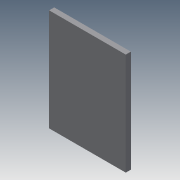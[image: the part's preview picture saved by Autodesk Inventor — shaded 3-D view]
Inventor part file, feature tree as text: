
AUTODESK INVENTOR PART (.ipt)
format: ipt  version: 2015 (Build 190159000, 159)  size: 68,608 bytes
history: native  units: mm
features: extrude x1, sketch x1
ambient origin geometry x8: Origin, YZ Plane, XZ Plane, XY Plane, X Axis, Y Axis, Z Axis, Center Point
bodies: Solid1 (feature_tree)
feature tree (2):
  extrude  "Extrusion1"  Depth=150.0mm
  sketch  "Sketch1"  dims[d0=200.0mm d1=150.0mm d2=10.0mm d3=0.0mm]
